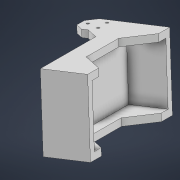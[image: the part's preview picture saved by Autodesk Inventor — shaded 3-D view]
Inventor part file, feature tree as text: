
AUTODESK INVENTOR PART (.ipt)
format: ipt  version: 2021 (Build 250183000, 183)  size: 321,024 bytes
history: native  units: mm
features: extrude x3, chamfer x3, sketch x3, mirror x1, plane x1
ambient origin geometry x8: Origin, YZ Plane, XZ Plane, XY Plane, X Axis, Y Axis, Z Axis, Center Point
bodies: Solid1 (feature_tree)
feature tree (11):
  extrude  "Extrusion1"  Depth=10.0mm
  extrude  "Extrusion2"  TaperAngle=135.0deg  [1 undecoded]
  mirror  "Mirror1"
  extrude  "Extrusion3"  Depth=6.0mm
  chamfer  "Chamfer1"  [1 undecoded]
  chamfer  "Chamfer2"  Distance=6.0mm
  chamfer  "Chamfer3"  Distance=6.0mm
  sketch  "Sketch1"  dims[d0=53.5mm d1=10.0mm]
  sketch  "Sketch2"  dims[d2=10.0mm d3=135.0deg]
  plane  "Work Plane1"
  sketch  "Sketch4"  dims[d4=30.0mm d5=6.0mm d6=0.0mm d7=6.0mm d8=6.0mm d9=6.0mm d10=31.0mm d11=0.0mm d26=25.0mm d27=26.0mm d30=12.0mm d33=6.0mm d34=0.0mm d35=7.5mm d36=2.0mm d37=45.0deg d38=13.0mm d39=15.0mm d40=2.5mm d41=30.0mm d43=360.0deg d45=12.5mm d46=2.0mm d47=45.0deg d48=3.0mm d49=2.0mm d50=45.0deg d42=0.25mm d44=14.3117mm]
note: 2 required parameter values undecoded (feature->parameter linkage not recoverable at this tier; creation-order binding heuristic only, values carry confidence <= 0.55)
